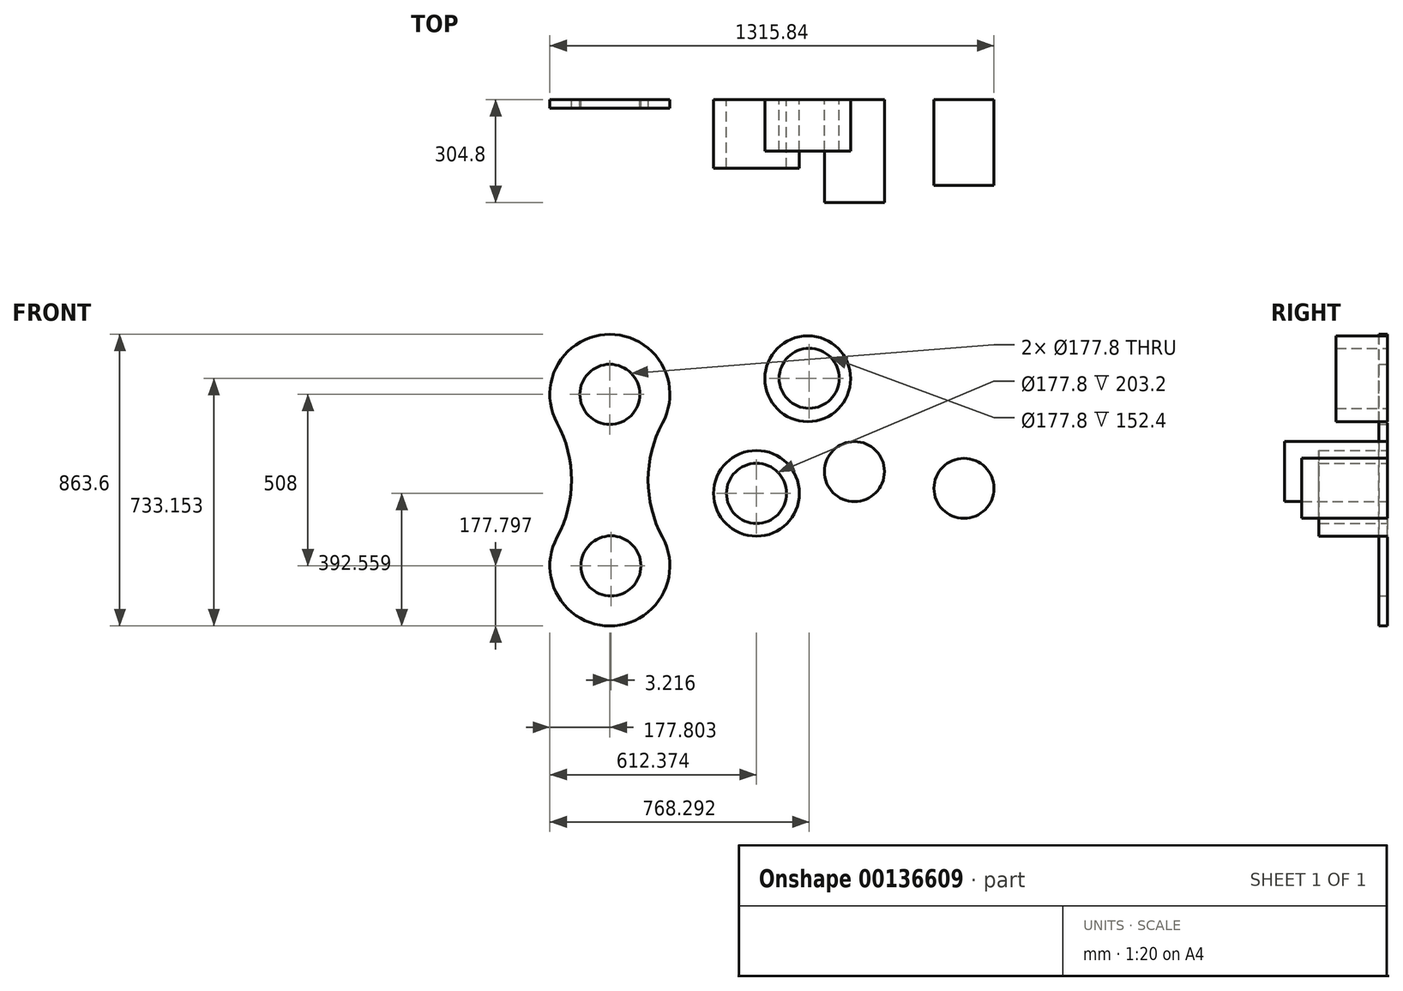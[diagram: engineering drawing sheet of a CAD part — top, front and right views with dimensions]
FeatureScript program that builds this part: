
annotation { "Feature Type Name" : "Feature", "Feature Type Description" : "" }
export const myFeature = defineFeature(function(context is Context, id is Id, definition is map)
    precondition{}
    {
        {
            var Q0;
            Q0=qCreatedBy(makeId("Front.planeOp"),FACE);
            var sketch = newSketch(context, id + "F0", { "sketchPlane" : qUnion([Q0])});
            skCircle(sketch, "E0", {"center": v(-19.97, 103.08) * mm, "radius": 88.9 * mm});
            skArc(sketch, "E1", {"start": v(136.38, 18.41) * mm, "mid": v(-19.97, 280.88) * mm, "end": v(-176.31, 18.41) * mm});
            skArc(sketch, "E2", {"start": v(-176.31, -320.26) * mm, "mid": v(-19.97, -582.72) * mm, "end": v(136.38, -320.26) * mm});
            skCircle(sketch, "E3", {"center": v(-16.75, -404.92) * mm, "radius": 88.9 * mm});
            skArc(sketch, "E4", {"start": v(-176.31, -320.26) * mm, "mid": v(-133.4, -150.92) * mm, "end": v(-176.31, 18.41) * mm});
            skArc(sketch, "E5", {"start": v(136.38, 18.41) * mm, "mid": v(93.47, -150.92) * mm, "end": v(136.38, -320.26) * mm});
            skSolve(sketch);
        }
        {
            var Q0;
            Q0=makeQuery(id+"F0.imprint","IMPRINT",FACE,{"disambiguationData":[TD([[makeQuery(id+"F0.imprint","IMPRINT",EDGE,{"derivedFrom":sQuery(id+"F0.wireOp",EDGE,"E0")}),-1.0]])]});
            extrude(context, id + "F1", {"entities" : qUnion([Q0]), "depth" : 25.4 * mm});
        }
        {
            var Q0;
            Q0=qCreatedBy(makeId("Front.planeOp"),FACE);
            var sketch = newSketch(context, id + "F2", { "sketchPlane" : qUnion([Q0])});
            skCircle(sketch, "E6", {"center": v(1029.17, -175.43) * mm, "radius": 88.9 * mm});
            skSolve(sketch);
        }
        {
            var Q0;
            Q0=makeQuery(id+"F2.imprint","IMPRINT",FACE,{"disambiguationData":[TD([[makeQuery(id+"F2.imprint","IMPRINT",EDGE,{"derivedFrom":sQuery(id+"F2.wireOp",EDGE,"E6")}),1.0]])]});
            extrude(context, id + "F3", {"entities" : qUnion([Q0]), "depth" : 254 * mm});
        }
        {
            var Q0;
            Q0=qCreatedBy(makeId("Front.planeOp"),FACE);
            var sketch = newSketch(context, id + "F4", { "sketchPlane" : qUnion([Q0])});
            skCircle(sketch, "E7", {"center": v(704.73, -125.78) * mm, "radius": 88.9 * mm});
            skSolve(sketch);
        }
        {
            var Q0;
            Q0=makeQuery(id+"F4.imprint","IMPRINT",FACE,{"disambiguationData":[TD([[makeQuery(id+"F4.imprint","IMPRINT",EDGE,{"derivedFrom":sQuery(id+"F4.wireOp",EDGE,"E7")}),1.0]])]});
            extrude(context, id + "F5", {"entities" : qUnion([Q0]), "depth" : 304.8 * mm});
        }
        {
            var Q0;
            Q0=qCreatedBy(makeId("Front.planeOp"),FACE);
            var sketch = newSketch(context, id + "F6", { "sketchPlane" : qUnion([Q0])});
            skCircle(sketch, "E8", {"center": v(566.46, 149.24) * mm, "radius": 127 * mm});
            skCircle(sketch, "E9", {"center": v(570.52, 150.43) * mm, "radius": 88.9 * mm});
            skSolve(sketch);
        }
        {
            var Q0;
            Q0=makeQuery(id+"F6.imprint","IMPRINT",FACE,{"disambiguationData":[TD([[makeQuery(id+"F6.imprint","IMPRINT",EDGE,{"derivedFrom":sQuery(id+"F6.wireOp",EDGE,"E8")}),1.0]])]});
            extrude(context, id + "F7", {"entities" : qUnion([Q0]), "depth" : 152.4 * mm});
        }
        {
            var Q0;
            Q0=qCreatedBy(makeId("Front.planeOp"),FACE);
            var sketch = newSketch(context, id + "F8", { "sketchPlane" : qUnion([Q0])});
            skCircle(sketch, "E10", {"center": v(414.6, -190.16) * mm, "radius": 127 * mm});
            skCircle(sketch, "E11", {"center": v(414.6, -190.16) * mm, "radius": 88.9 * mm});
            skSolve(sketch);
        }
        {
            var Q0;
            Q0=makeQuery(id+"F8.imprint","IMPRINT",FACE,{"disambiguationData":[TD([[makeQuery(id+"F8.imprint","IMPRINT",EDGE,{"derivedFrom":sQuery(id+"F8.wireOp",EDGE,"E10")}),1.0]])]});
            extrude(context, id + "F9", {"entities" : qUnion([Q0]), "depth" : 203.2 * mm});
        }
    });
